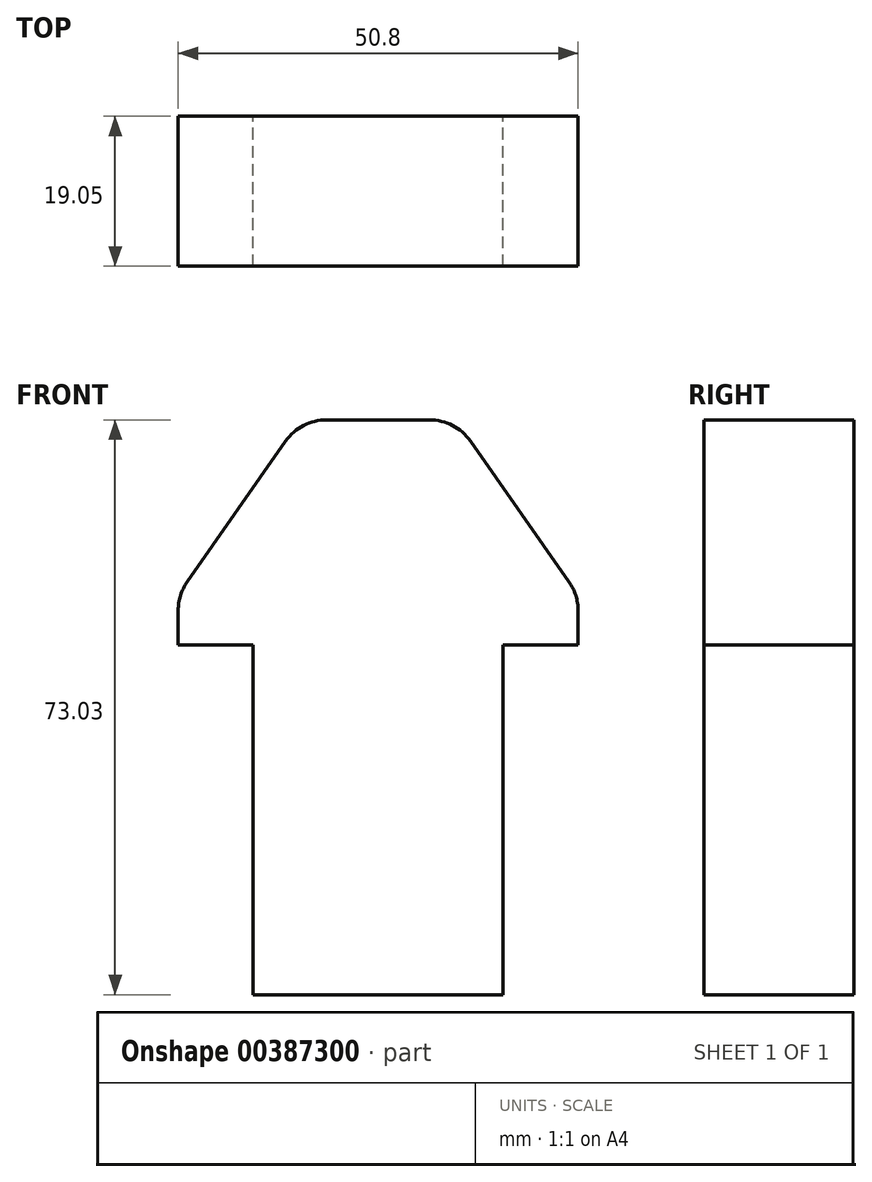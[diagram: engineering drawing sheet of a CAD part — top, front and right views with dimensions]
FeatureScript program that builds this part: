
annotation { "Feature Type Name" : "Feature", "Feature Type Description" : "" }
export const myFeature = defineFeature(function(context is Context, id is Id, definition is map)
    precondition{}
    {
        {
            var Q0;
            Q0=qCreatedBy(makeId("Front.planeOp"),FACE);
            var sketch = newSketch(context, id + "F0", { "sketchPlane" : qUnion([Q0])});
            skLineSegment(sketch, "E0", {"start": v(0, 0) * mm, "end": v(-15.88, 0) * mm});
            skLineSegment(sketch, "E1", {"start": v(-15.88, 0) * mm, "end": v(-15.88, 44.45) * mm});
            skLineSegment(sketch, "E2", {"start": v(-15.88, 44.45) * mm, "end": v(-25.4, 44.45) * mm});
            skLineSegment(sketch, "E3", {"start": v(-25.4, 44.45) * mm, "end": v(-25.4, 48.8) * mm});
            skLineSegment(sketch, "E4", {"start": v(-24.25, 52.44) * mm, "end": v(-11.73, 70.32) * mm});
            skLineSegment(sketch, "E5", {"start": v(-6.53, 73.02) * mm, "end": v(0, 73.02) * mm});
            skLineSegment(sketch, "E6", {"start": v(0, 73.03) * mm, "end": v(0, 0) * mm, "construction": true});
            skLineSegment(sketch, "E7.MirrorCS", {"start": v(6.53, 73.03) * mm, "end": v(0, 73.03) * mm});
            skLineSegment(sketch, "E8.MirrorCS", {"start": v(24.25, 52.44) * mm, "end": v(11.73, 70.32) * mm});
            skLineSegment(sketch, "E9.MirrorCS", {"start": v(25.4, 44.45) * mm, "end": v(25.4, 48.8) * mm});
            skLineSegment(sketch, "E10.MirrorCS", {"start": v(15.87, 44.45) * mm, "end": v(25.4, 44.45) * mm});
            skLineSegment(sketch, "E11.MirrorCS", {"start": v(15.88, 0) * mm, "end": v(15.87, 44.45) * mm});
            skLineSegment(sketch, "E12.MirrorCS", {"start": v(0, 0) * mm, "end": v(15.88, 0) * mm});
            skPoint(sketch, "E13.visualSharp", {"position": v(25.4, 50.8) * mm});
            skArc(sketch, "E13.filletArc", {"start": v(25.4, 48.8) * mm, "mid": v(25.1, 50.7) * mm, "end": v(24.25, 52.44) * mm});
            skPoint(sketch, "E14.visualSharp", {"position": v(9.84, 73.03) * mm});
            skArc(sketch, "E14.filletArc", {"start": v(11.73, 70.32) * mm, "mid": v(9.46, 72.3) * mm, "end": v(6.53, 73.02) * mm});
            skPoint(sketch, "E15.visualSharp", {"position": v(-9.84, 73.03) * mm});
            skArc(sketch, "E15.filletArc", {"start": v(-6.53, 73.02) * mm, "mid": v(-9.46, 72.3) * mm, "end": v(-11.73, 70.32) * mm});
            skPoint(sketch, "E16.visualSharp", {"position": v(-25.4, 50.8) * mm});
            skArc(sketch, "E16.filletArc", {"start": v(-24.25, 52.44) * mm, "mid": v(-25.1, 50.7) * mm, "end": v(-25.4, 48.8) * mm});
            skSolve(sketch);
        }
        {
            var Q0;
            Q0 = qSketchRegion(id + "F0", true);
            extrude(context, id + "F1", {"entities" : qUnion([Q0]), "depth" : 19.05 * mm});
        }
    });
